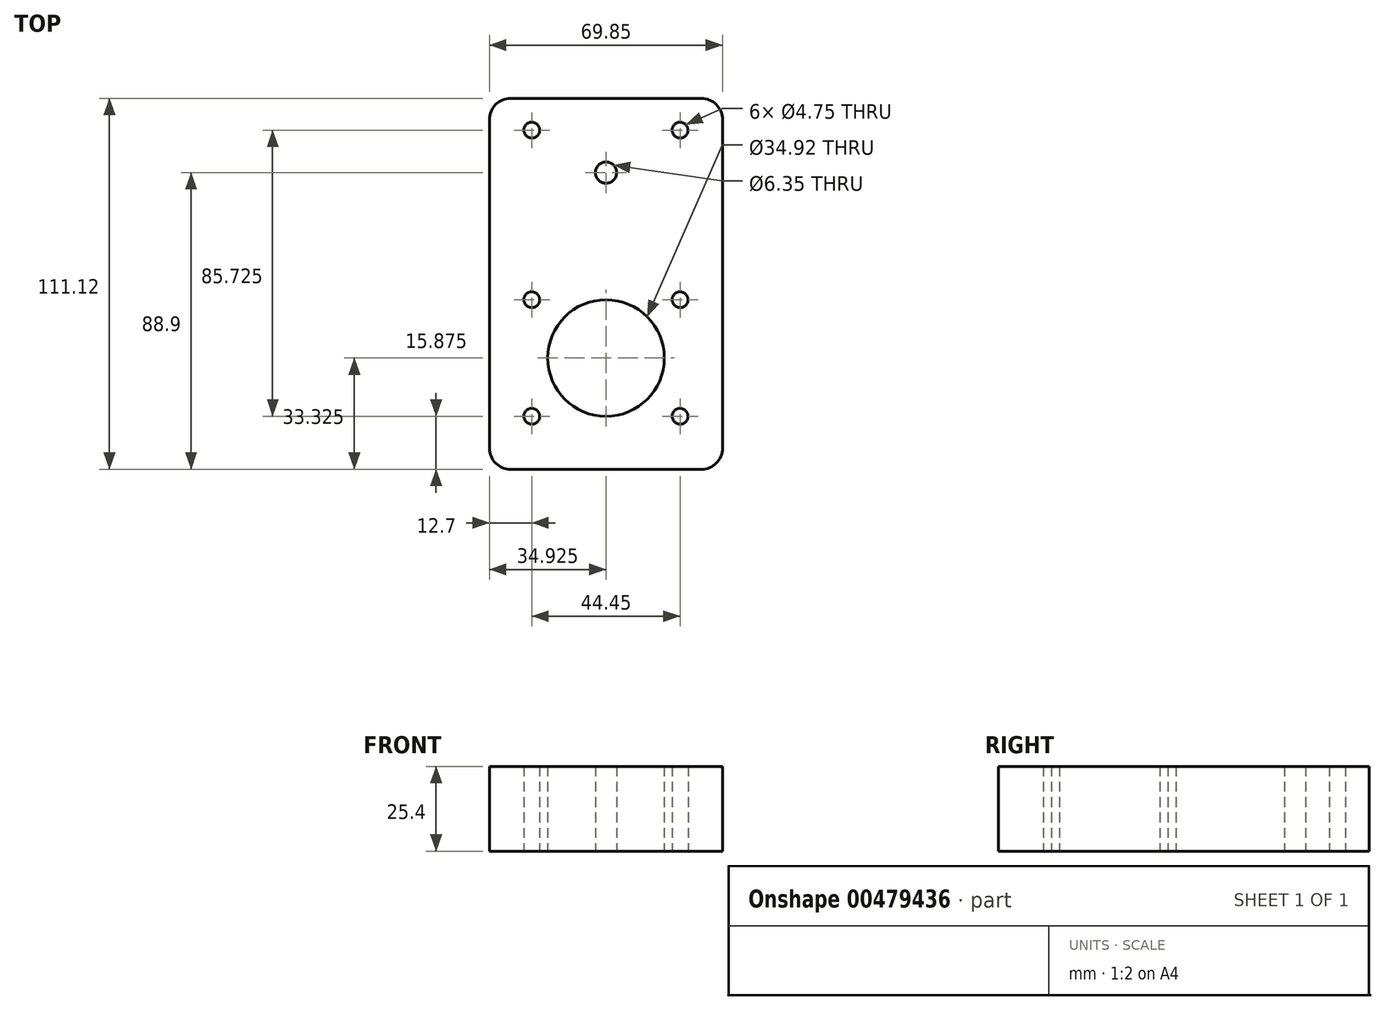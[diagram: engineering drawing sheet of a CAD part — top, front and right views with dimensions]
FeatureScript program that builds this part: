
annotation { "Feature Type Name" : "Feature", "Feature Type Description" : "" }
export const myFeature = defineFeature(function(context is Context, id is Id, definition is map)
    precondition{}
    {
        {
            var Q0;
            Q0=qCreatedBy(makeId("Top.planeOp"),FACE);
            var sketch = newSketch(context, id + "F0", { "sketchPlane" : qUnion([Q0]), "disableImprinting" : false});
            skLineSegment(sketch, "E0.bottom", {"start": v(6.35, 0) * mm, "end": v(63.5, 0) * mm});
            skLineSegment(sketch, "E0.top", {"start": v(6.35, 111.13) * mm, "end": v(63.5, 111.13) * mm});
            skLineSegment(sketch, "E0.left", {"start": v(0, 6.35) * mm, "end": v(0, 104.78) * mm});
            skLineSegment(sketch, "E0.right", {"start": v(69.85, 6.35) * mm, "end": v(69.85, 104.78) * mm});
            skCircle(sketch, "E1", {"center": v(12.7, 15.88) * mm, "radius": 2.37 * mm});
            skCircle(sketch, "E2", {"center": v(57.15, 15.88) * mm, "radius": 2.37 * mm});
            skCircle(sketch, "E3", {"center": v(34.93, 33.32) * mm, "radius": 17.46 * mm});
            skCircle(sketch, "E4", {"center": v(12.7, 50.8) * mm, "radius": 2.37 * mm});
            skCircle(sketch, "E5", {"center": v(57.15, 50.8) * mm, "radius": 2.37 * mm});
            skCircle(sketch, "E6", {"center": v(12.7, 101.6) * mm, "radius": 2.37 * mm});
            skCircle(sketch, "E7", {"center": v(34.92, 88.9) * mm, "radius": 3.18 * mm});
            skCircle(sketch, "E8", {"center": v(57.15, 101.6) * mm, "radius": 2.37 * mm});
            skPoint(sketch, "E9.visualSharp", {"position": v(0, 111.13) * mm});
            skArc(sketch, "E9.filletArc", {"start": v(6.35, 111.13) * mm, "mid": v(1.86, 109.27) * mm, "end": v(0, 104.78) * mm});
            skPoint(sketch, "E10.visualSharp", {"position": v(69.85, 111.13) * mm});
            skArc(sketch, "E10.filletArc", {"start": v(69.85, 104.78) * mm, "mid": v(68, 109.27) * mm, "end": v(63.5, 111.13) * mm});
            skPoint(sketch, "E11.visualSharp", {"position": v(69.85, 0) * mm});
            skArc(sketch, "E11.filletArc", {"start": v(63.5, 0) * mm, "mid": v(68, 1.86) * mm, "end": v(69.85, 6.35) * mm});
            skPoint(sketch, "E12.visualSharp", {"position": v(0, 0) * mm});
            skArc(sketch, "E12.filletArc", {"start": v(0, 6.35) * mm, "mid": v(1.86, 1.86) * mm, "end": v(6.35, 0) * mm});
            skSolve(sketch);
        }
        {
            var Q0;
            Q0 = qSketchRegion(id + "F0", true);
            extrude(context, id + "F1", {"entities" : qUnion([Q0]), "depth" : 25.4 * mm});
        }
    });
